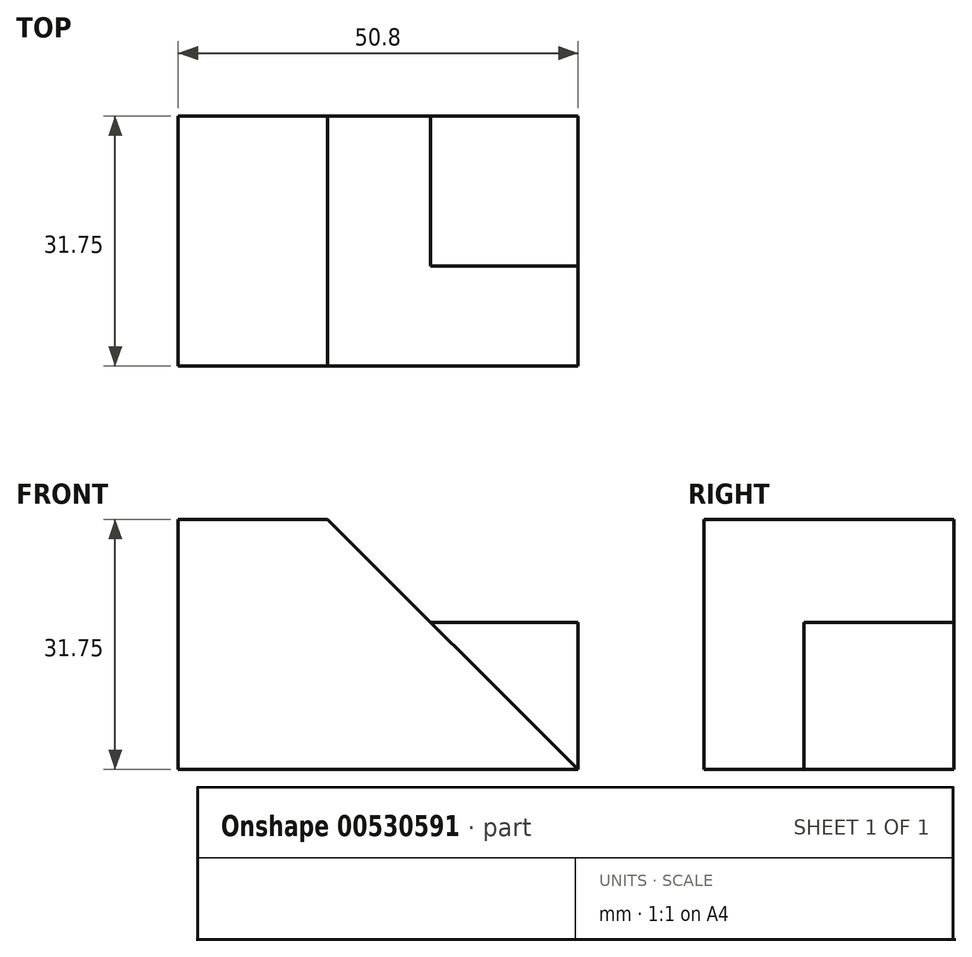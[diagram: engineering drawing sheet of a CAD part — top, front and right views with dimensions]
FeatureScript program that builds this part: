
annotation { "Feature Type Name" : "Feature", "Feature Type Description" : "" }
export const myFeature = defineFeature(function(context is Context, id is Id, definition is map)
    precondition{}
    {
        {
            var Q0;
            Q0=qCreatedBy(makeId("Front.planeOp"),FACE);
            var sketch = newSketch(context, id + "F0", { "sketchPlane" : qUnion([Q0])});
            skLineSegment(sketch, "E0", {"start": v(-63.7, 40.7) * mm, "end": v(-63.7, 8.94) * mm});
            skLineSegment(sketch, "E1", {"start": v(-63.7, 8.94) * mm, "end": v(-12.9, 8.94) * mm});
            skLineSegment(sketch, "E2", {"start": v(-12.9, 8.94) * mm, "end": v(-12.9, 40.7) * mm});
            skLineSegment(sketch, "E3", {"start": v(-12.9, 40.7) * mm, "end": v(-63.7, 40.7) * mm});
            skSolve(sketch);
        }
        {
            var Q0;
            Q0=makeQuery(id+"F0.imprint","IMPRINT",FACE,{"disambiguationData":[TD([[makeQuery(id+"F0.imprint","IMPRINT",EDGE,{"derivedFrom":sQuery(id+"F0.wireOp",EDGE,"E0")}),1.0]])]});
            extrude(context, id + "F1", {"entities" : qUnion([Q0]), "depth" : 31.75 * mm, "offsetDistance" : 25.4 * mm});
        }
        {
            var Q0;
            Q0=makeQuery(id+"F1.opExtrude","CAP_FACE",FACE,{"disambiguationData":[OSD([sQuery(id+"F0.wireOp",EDGE,"E0"),sQuery(id+"F0.wireOp",EDGE,"E1"),sQuery(id+"F0.wireOp",EDGE,"E2"),sQuery(id+"F0.wireOp",EDGE,"E3")])],"isStart":false});
            var sketch = newSketch(context, id + "F2", { "sketchPlane" : qUnion([Q0])});
            skLineSegment(sketch, "E4", {"start": v(-12.9, 40.7) * mm, "end": v(-44.71, 40.7) * mm});
            skLineSegment(sketch, "E5", {"start": v(-44.71, 40.7) * mm, "end": v(-12.9, 8.94) * mm});
            skLineSegment(sketch, "E6", {"start": v(-12.9, 8.94) * mm, "end": v(-12.9, 40.7) * mm});
            skSolve(sketch);
        }
        {
            var Q0;
            Q0=makeQuery(id+"F2.imprint","IMPRINT",FACE,{"disambiguationData":[TD([[makeQuery(id+"F2.imprint","IMPRINT",EDGE,{"derivedFrom":sQuery(id+"F2.wireOp",EDGE,"E4")}),1.0]])]});
            extrude(context, id + "F3", {"entities" : qUnion([Q0]), "operationType" : NewBodyOperationType.REMOVE, "oppositeDirection" : true, "depth" : 12.7 * mm, "offsetDistance" : 25.4 * mm});
        }
        {
            var Q0;
            Q0=makeQuery(id+"F3.boolean.opBoolean","COPY",FACE,{"derivedFrom":makeQuery(id+"F3.opExtrude","CAP_FACE",FACE,{"disambiguationData":[OSD([sQuery(id+"F2.wireOp",EDGE,"E4"),sQuery(id+"F2.wireOp",EDGE,"E5"),sQuery(id+"F2.wireOp",EDGE,"E6")])],"isStart":false})});
            var sketch = newSketch(context, id + "F4", { "sketchPlane" : qUnion([Q0])});
            skLineSegment(sketch, "E7", {"start": v(-12.9, 8.94) * mm, "end": v(-12.9, 27.64) * mm});
            skLineSegment(sketch, "E8", {"start": v(-12.9, 27.64) * mm, "end": v(-31.63, 27.64) * mm});
            skSolve(sketch);
        }
        {
            var Q0;
            {var subQ0=sQuery(id+"F4.wireOp",EDGE,"E8");Q0=makeQuery(id+"F4.imprint","IMPRINT",FACE,{"disambiguationData":[TD([[makeQuery(id+"F4.imprint","IMPRINT",EDGE,{"derivedFrom":subQ0}),-1.0]])]});}
            extrude(context, id + "F5", {"entities" : qUnion([Q0]), "operationType" : NewBodyOperationType.REMOVE, "oppositeDirection" : true, "depth" : 25.4 * mm, "offsetDistance" : 25.4 * mm});
        }
    });
